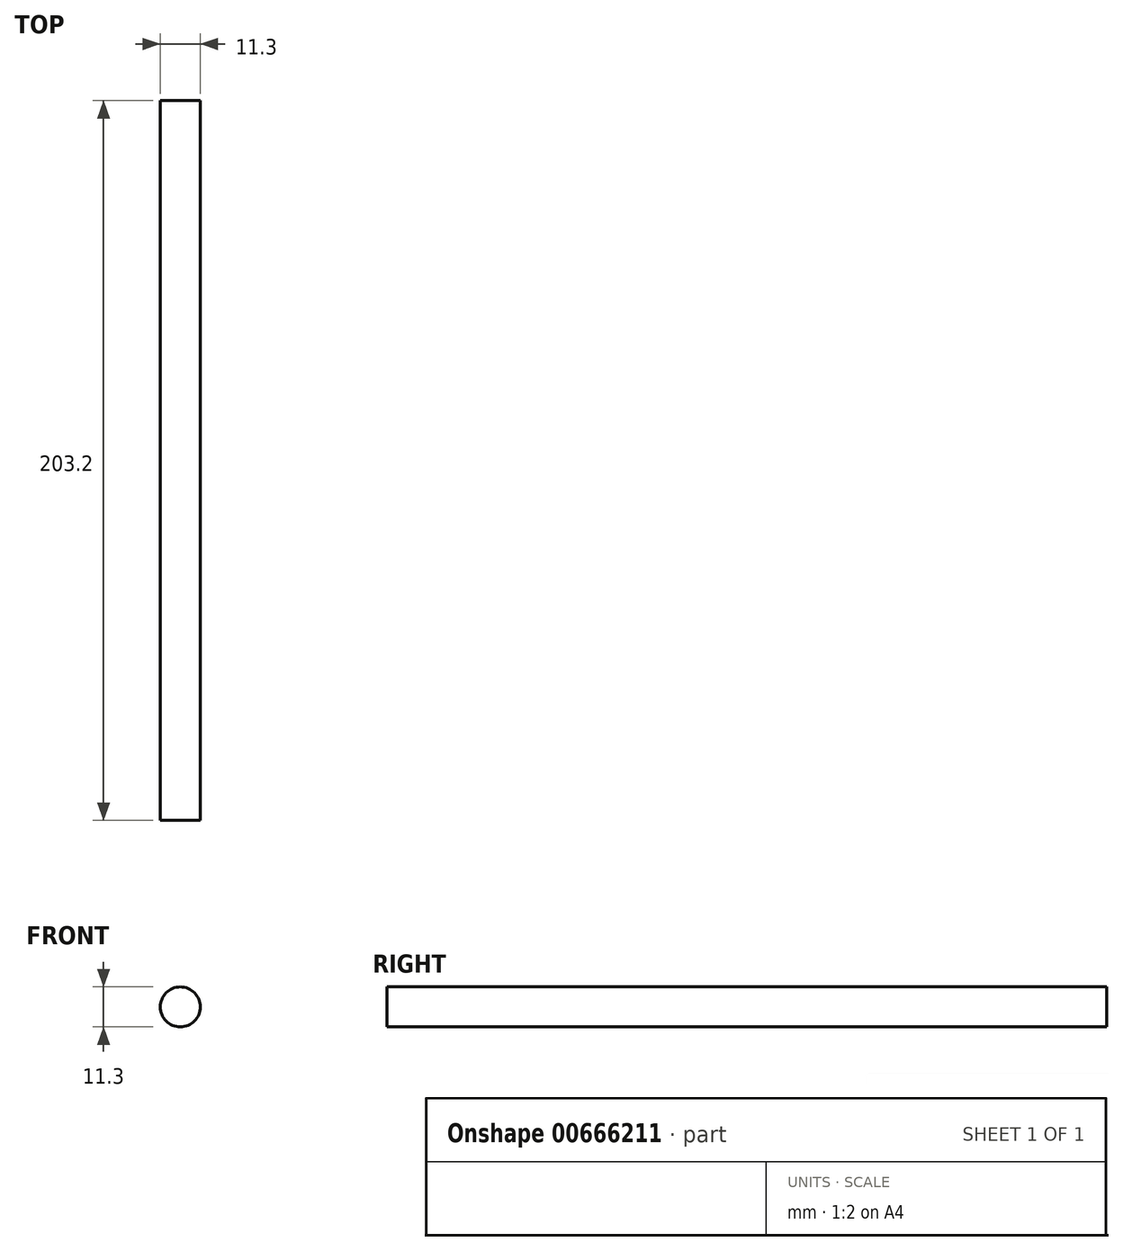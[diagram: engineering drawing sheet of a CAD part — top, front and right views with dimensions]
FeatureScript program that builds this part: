
annotation { "Feature Type Name" : "Feature", "Feature Type Description" : "" }
export const myFeature = defineFeature(function(context is Context, id is Id, definition is map)
    precondition{}
    {
        {
            var Q0;
            Q0=qCreatedBy(makeId("Front.planeOp"),FACE);
            var sketch = newSketch(context, id + "F0", { "sketchPlane" : qUnion([Q0])});
            skCircle(sketch, "E0", {"center": v(0, 0) * mm, "radius": 5.65 * mm});
            skSolve(sketch);
        }
        {
            var Q0;
            Q0=makeQuery(id+"F0.imprint","IMPRINT",FACE,{"disambiguationData":[TD([[makeQuery(id+"F0.imprint","IMPRINT",EDGE,{"derivedFrom":sQuery(id+"F0.wireOp",EDGE,"E0")}),1.0]])]});
            extrude(context, id + "F1", {"entities" : qUnion([Q0]), "depth" : 101.6 * mm, "offsetDistance" : 25.4 * mm, "hasSecondDirection" : true, "secondDirectionOppositeDirection" : true, "secondDirectionDepth" : 101.6 * mm});
        }
    });
